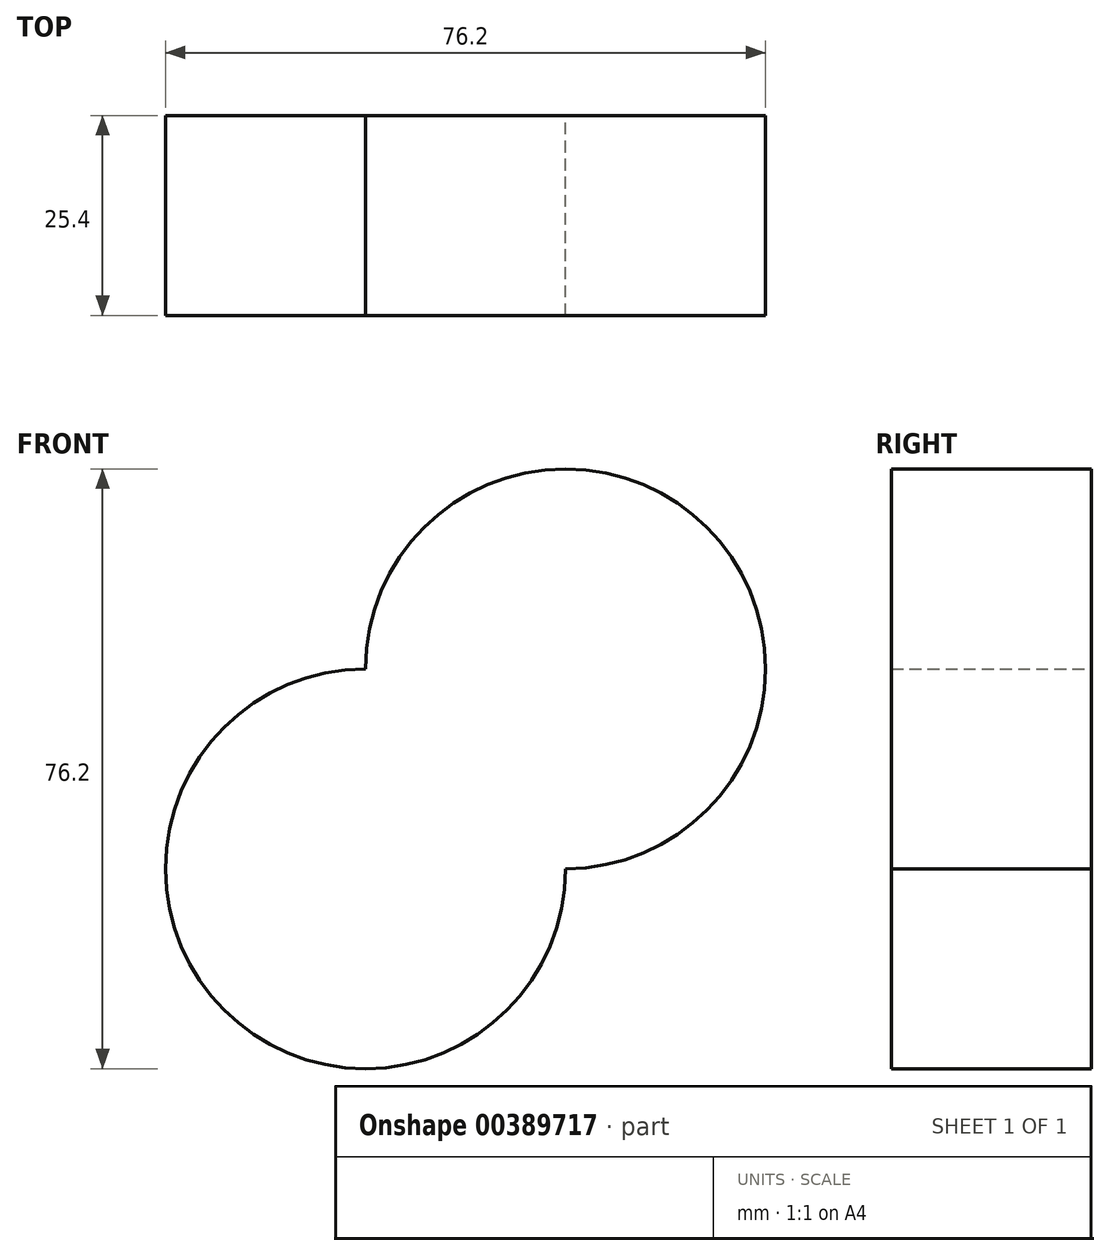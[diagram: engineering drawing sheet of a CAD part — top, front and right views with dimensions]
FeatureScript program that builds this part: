
annotation { "Feature Type Name" : "Feature", "Feature Type Description" : "" }
export const myFeature = defineFeature(function(context is Context, id is Id, definition is map)
    precondition{}
    {
        {
            var Q0;
            Q0=qCreatedBy(makeId("Front.planeOp"),FACE);
            var sketch = newSketch(context, id + "F0", { "sketchPlane" : qUnion([Q0])});
            skArc(sketch, "E0", {"start": v(0, 25.4) * mm, "mid": v(-17.96, -17.96) * mm, "end": v(25.4, 0) * mm});
            skLineSegment(sketch, "E1", {"start": v(0, 25.4) * mm, "end": v(25.4, 0) * mm});
            skSolve(sketch);
        }
        {
            var Q0;
            Q0 = qSketchRegion(id + "F0", true);
            extrude(context, id + "F1", {"entities" : qUnion([Q0]), "depth" : 25.4 * mm});
        }
        {
            var Q0;
            Q0=makeQuery(id+"F1.opExtrude","SWEPT_BODY",BODY,{"disambiguationData":[OSD([sQuery(id+"F0.wireOp",EDGE,"E0"),sQuery(id+"F0.wireOp",EDGE,"E1")])]});
            var Q1;
            Q1=makeQuery(id+"F1.opExtrude","SWEPT_FACE",FACE,{"disambiguationData":[OSD([sQuery(id+"F0.wireOp",EDGE,"E1")])]});
            mirror(context, id + "F2", {"operationType" : NewBodyOperationType.ADD, "entities" : qUnion([Q0]), "mirrorPlane" : qUnion([Q1])});
        }
    });
